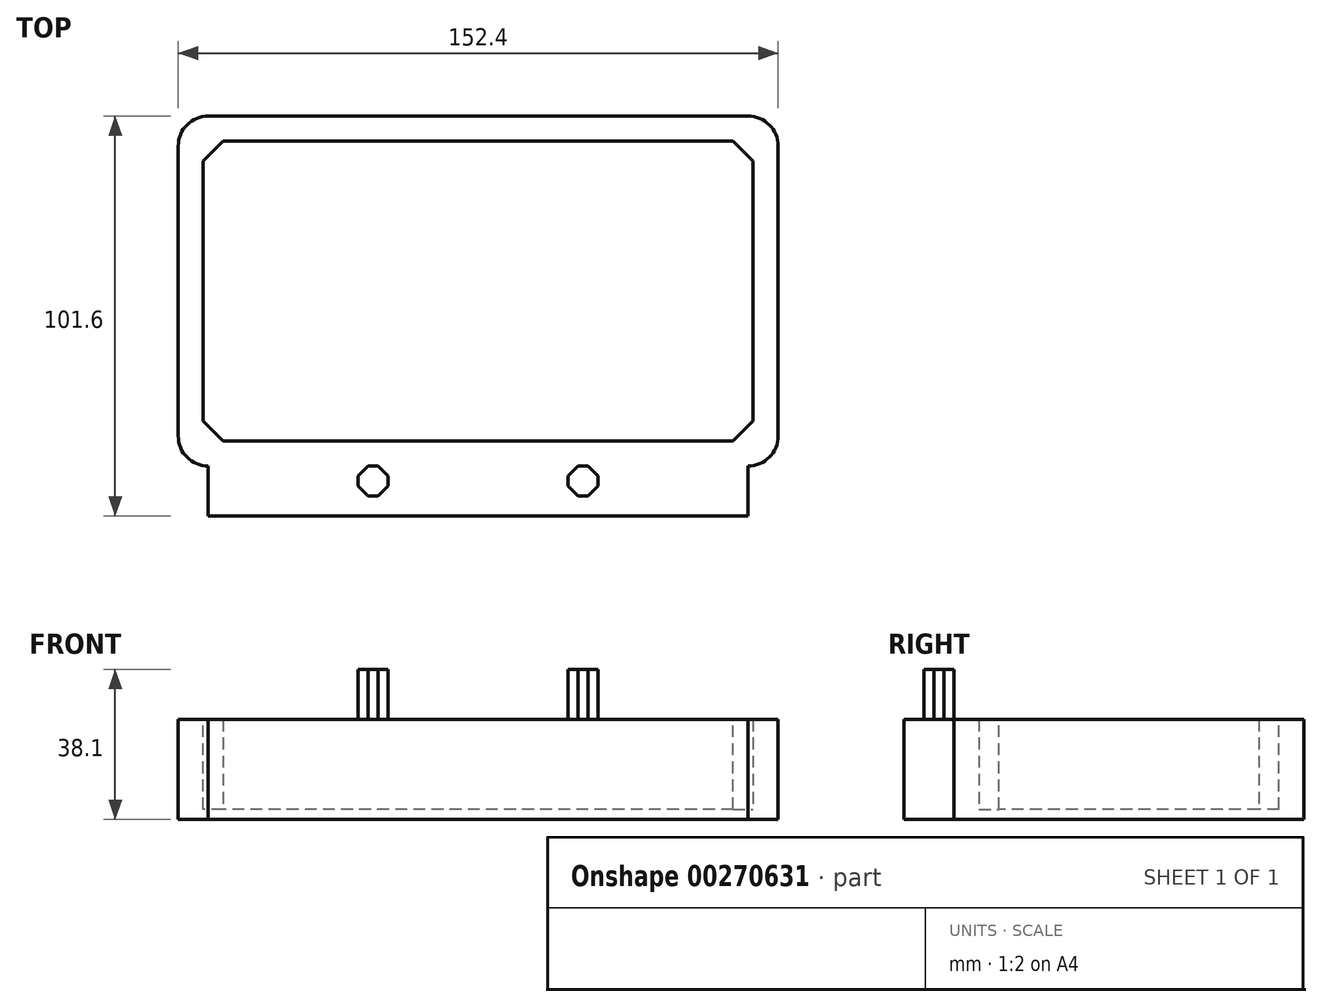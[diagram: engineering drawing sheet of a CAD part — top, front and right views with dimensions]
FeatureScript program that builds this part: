
annotation { "Feature Type Name" : "Feature", "Feature Type Description" : "" }
export const myFeature = defineFeature(function(context is Context, id is Id, definition is map)
    precondition{}
    {
        {
            var Q0;
            Q0=qCreatedBy(makeId("Top.planeOp"),FACE);
            var sketch = newSketch(context, id + "F0", { "sketchPlane" : qUnion([Q0])});
            skLineSegment(sketch, "E0.bottom", {"start": v(68.58, 44.45) * mm, "end": v(-68.58, 44.45) * mm});
            skLineSegment(sketch, "E0.top", {"start": v(68.58, -44.45) * mm, "end": v(-68.58, -44.45) * mm});
            skLineSegment(sketch, "E0.left", {"start": v(76.2, 36.83) * mm, "end": v(76.2, -36.83) * mm});
            skLineSegment(sketch, "E0.right", {"start": v(-76.2, 36.83) * mm, "end": v(-76.2, -36.83) * mm});
            skPoint(sketch, "E0.middle", {"position": v(0, 0) * mm});
            skLineSegment(sketch, "E1.bottom", {"start": v(69.85, 38.1) * mm, "end": v(-69.85, 38.1) * mm});
            skLineSegment(sketch, "E1.top", {"start": v(69.85, -38.1) * mm, "end": v(-69.85, -38.1) * mm});
            skLineSegment(sketch, "E1.left", {"start": v(69.85, 38.1) * mm, "end": v(69.85, -38.1) * mm});
            skLineSegment(sketch, "E1.right", {"start": v(-69.85, 38.1) * mm, "end": v(-69.85, -38.1) * mm});
            skPoint(sketch, "E2.visualSharp", {"position": v(-69.85, 38.1) * mm});
            skPoint(sketch, "E3.visualSharp", {"position": v(-69.85, -38.1) * mm});
            skLineSegment(sketch, "E3.filletArc", {"start": v(-69.85, -38.1) * mm, "end": v(-69.85, -38.1) * mm});
            skPoint(sketch, "E4.visualSharp", {"position": v(69.85, -38.1) * mm});
            skLineSegment(sketch, "E4.filletArc", {"start": v(69.85, -38.1) * mm, "end": v(69.85, -38.1) * mm});
            skPoint(sketch, "E5.visualSharp", {"position": v(69.85, 38.1) * mm});
            skLineSegment(sketch, "E5.filletArc", {"start": v(69.85, 38.1) * mm, "end": v(69.85, 38.1) * mm});
            skPoint(sketch, "E6.visualSharp", {"position": v(-76.2, 44.45) * mm});
            skArc(sketch, "E6.filletArc", {"start": v(-68.58, 44.45) * mm, "mid": v(-73.97, 42.22) * mm, "end": v(-76.2, 36.83) * mm});
            skPoint(sketch, "E7.visualSharp", {"position": v(76.2, 44.45) * mm});
            skArc(sketch, "E7.filletArc", {"start": v(76.2, 36.83) * mm, "mid": v(73.97, 42.22) * mm, "end": v(68.58, 44.45) * mm});
            skPoint(sketch, "E8.visualSharp", {"position": v(-76.2, -44.45) * mm});
            skArc(sketch, "E8.filletArc", {"start": v(-76.2, -36.83) * mm, "mid": v(-73.97, -42.22) * mm, "end": v(-68.58, -44.45) * mm});
            skPoint(sketch, "E9.visualSharp", {"position": v(76.2, -44.45) * mm});
            skArc(sketch, "E9.filletArc", {"start": v(68.58, -44.45) * mm, "mid": v(73.97, -42.22) * mm, "end": v(76.2, -36.83) * mm});
            skSolve(sketch);
        }
        {
            var Q0;
            Q0=makeQuery(id+"F0.imprint","IMPRINT",FACE,{"disambiguationData":[TD([[makeQuery(id+"F0.imprint","IMPRINT",EDGE,{"derivedFrom":sQuery(id+"F0.wireOp",EDGE,"E0.bottom")}),1.0]])]});
            extrude(context, id + "F1", {"entities" : qUnion([Q0]), "depth" : 25.4 * mm});
        }
        {
            var Q0;
            Q0=makeQuery(id+"F1.opExtrude","SWEPT_EDGE",EDGE,{"disambiguationData":[OSD([sQuery(id+"F0.wireOp",EDGE,"E1.bottom"),sQuery(id+"F0.wireOp",EDGE,"E1.right")])]});
            var Q1;
            Q1=makeQuery(id+"F1.opExtrude","SWEPT_EDGE",EDGE,{"disambiguationData":[OSD([sQuery(id+"F0.wireOp",EDGE,"E1.top"),sQuery(id+"F0.wireOp",EDGE,"E1.right")])]});
            var Q2;
            Q2=makeQuery(id+"F1.opExtrude","SWEPT_EDGE",EDGE,{"disambiguationData":[OSD([sQuery(id+"F0.wireOp",EDGE,"E1.bottom"),sQuery(id+"F0.wireOp",EDGE,"E1.left")])]});
            var Q3;
            Q3=makeQuery(id+"F1.opExtrude","SWEPT_EDGE",EDGE,{"disambiguationData":[OSD([sQuery(id+"F0.wireOp",EDGE,"E1.top"),sQuery(id+"F0.wireOp",EDGE,"E1.left")])]});
            chamfer(context, id + "F2", {"entities" : qUnion([Q0, Q1, Q2, Q3]), "width" : 5.08 * mm, "tangentPropagation" : true});
        }
        {
            var Q0;
            Q0=qCreatedBy(makeId("Top.planeOp"),FACE);
            var sketch = newSketch(context, id + "F3", { "sketchPlane" : qUnion([Q0])});
            skLineSegment(sketch, "E10.bottom", {"start": v(-72.19, -40.25) * mm, "end": v(72.1, -40.25) * mm});
            skLineSegment(sketch, "E10.top", {"start": v(-72.19, 41.27) * mm, "end": v(72.1, 41.27) * mm});
            skLineSegment(sketch, "E10.left", {"start": v(-72.19, -40.25) * mm, "end": v(-72.19, 41.27) * mm});
            skLineSegment(sketch, "E10.right", {"start": v(72.1, -40.25) * mm, "end": v(72.1, 41.27) * mm});
            skSolve(sketch);
        }
        {
            var Q0;
            Q0 = qSketchRegion(id + "F3", true);
            extrude(context, id + "F4", {"entities" : qUnion([Q0]), "operationType" : NewBodyOperationType.ADD, "depth" : 2.54 * mm});
        }
        {
            var Q0;
            Q0=makeQuery(id+"F1.opExtrude","SWEPT_FACE",FACE,{"disambiguationData":[OSD([sQuery(id+"F0.wireOp",EDGE,"E0.top")])]});
            extrude(context, id + "F5", {"entities" : qUnion([Q0]), "operationType" : NewBodyOperationType.ADD, "depth" : 12.7 * mm});
        }
        {
            var Q0;
            {var subQ0=sQuery(id+"F0.wireOp",EDGE,"E0.top");Q0=makeQuery(id+"F5.boolean.opBoolean","MERGE",FACE,{"derivedFrom":[makeQuery(id+"F1.opExtrude","CAP_FACE",FACE,{"disambiguationData":[OSD([sQuery(id+"F0.wireOp",EDGE,"E0.bottom"),subQ0,sQuery(id+"F0.wireOp",EDGE,"E0.left"),sQuery(id+"F0.wireOp",EDGE,"E0.right"),sQuery(id+"F0.wireOp",EDGE,"E1.bottom"),sQuery(id+"F0.wireOp",EDGE,"E1.top"),sQuery(id+"F0.wireOp",EDGE,"E1.left"),sQuery(id+"F0.wireOp",EDGE,"E1.right"),sQuery(id+"F0.wireOp",EDGE,"E6.filletArc"),sQuery(id+"F0.wireOp",EDGE,"E7.filletArc"),sQuery(id+"F0.wireOp",EDGE,"E8.filletArc"),sQuery(id+"F0.wireOp",EDGE,"E9.filletArc")])],"isStart":false}),makeQuery(id+"F5.opExtrude","SWEPT_FACE",FACE,{"disambiguationData":[OSD([subQ0]),TDD([makeQuery(id+"F1.opExtrude","CAP_EDGE",EDGE,{"disambiguationData":[OSD([subQ0])],"isStart":false})])]})]});}
            var sketch = newSketch(context, id + "F6", { "sketchPlane" : qUnion([Q0])});
            skLineSegment(sketch, "E11", {"start": v(68.58, -44.45) * mm, "end": v(30.48, -44.45) * mm});
            skLineSegment(sketch, "E12", {"start": v(-68.58, -44.45) * mm, "end": v(-30.48, -44.45) * mm});
            skLineSegment(sketch, "E13.bottom", {"start": v(30.48, -44.45) * mm, "end": v(22.86, -44.45) * mm});
            skLineSegment(sketch, "E13.top", {"start": v(30.48, -52.07) * mm, "end": v(22.86, -52.07) * mm});
            skLineSegment(sketch, "E13.left", {"start": v(30.48, -44.45) * mm, "end": v(30.48, -52.07) * mm});
            skLineSegment(sketch, "E13.right", {"start": v(22.86, -44.45) * mm, "end": v(22.86, -52.07) * mm});
            skLineSegment(sketch, "E14.bottom", {"start": v(-30.48, -44.45) * mm, "end": v(-22.86, -44.45) * mm});
            skLineSegment(sketch, "E14.top", {"start": v(-30.48, -52.07) * mm, "end": v(-22.86, -52.07) * mm});
            skLineSegment(sketch, "E14.left", {"start": v(-30.48, -44.45) * mm, "end": v(-30.48, -52.07) * mm});
            skLineSegment(sketch, "E14.right", {"start": v(-22.86, -44.45) * mm, "end": v(-22.86, -52.07) * mm});
            skSolve(sketch);
        }
        {
            var Q0;
            Q0=makeQuery(id+"F6.imprint","IMPRINT",FACE,{"disambiguationData":[TD([[makeQuery(id+"F6.imprint","IMPRINT",EDGE,{"derivedFrom":sQuery(id+"F6.wireOp",EDGE,"E13.bottom")}),1.0]])]});
            var Q1;
            Q1=makeQuery(id+"F6.imprint","IMPRINT",FACE,{"disambiguationData":[TD([[makeQuery(id+"F6.imprint","IMPRINT",EDGE,{"derivedFrom":sQuery(id+"F6.wireOp",EDGE,"E14.bottom")}),-1.0]])]});
            extrude(context, id + "F7", {"entities" : qUnion([Q0, Q1]), "operationType" : NewBodyOperationType.ADD, "depth" : 12.7 * mm});
        }
        {
            var Q0;
            Q0=makeQuery(id+"F7.opExtrude","SWEPT_EDGE",EDGE,{"disambiguationData":[OSD([sQuery(id+"F6.wireOp",EDGE,"E13.bottom"),sQuery(id+"F6.wireOp",EDGE,"E13.left")])]});
            chamfer(context, id + "F8", {"entities" : qUnion([Q0]), "width" : 2.54 * mm, "tangentPropagation" : true});
        }
        {
            var Q0;
            Q0=makeQuery(id+"F7.opExtrude","SWEPT_EDGE",EDGE,{"disambiguationData":[OSD([sQuery(id+"F6.wireOp",EDGE,"E13.bottom"),sQuery(id+"F6.wireOp",EDGE,"E13.right")])]});
            var Q1;
            Q1=makeQuery(id+"F7.opExtrude","SWEPT_EDGE",EDGE,{"disambiguationData":[OSD([sQuery(id+"F6.wireOp",EDGE,"E13.top"),sQuery(id+"F6.wireOp",EDGE,"E13.right")])]});
            chamfer(context, id + "F9", {"entities" : qUnion([Q0, Q1]), "width" : 2.54 * mm, "tangentPropagation" : true});
        }
        {
            var Q0;
            Q0=makeQuery(id+"F7.opExtrude","SWEPT_EDGE",EDGE,{"disambiguationData":[OSD([sQuery(id+"F6.wireOp",EDGE,"E13.top"),sQuery(id+"F6.wireOp",EDGE,"E13.left")])]});
            chamfer(context, id + "F10", {"entities" : qUnion([Q0]), "width" : 2.54 * mm, "tangentPropagation" : true});
        }
        {
            var Q0;
            Q0=makeQuery(id+"F7.opExtrude","SWEPT_EDGE",EDGE,{"disambiguationData":[OSD([sQuery(id+"F6.wireOp",EDGE,"E14.bottom"),sQuery(id+"F6.wireOp",EDGE,"E14.left")])]});
            var Q1;
            Q1=makeQuery(id+"F7.opExtrude","SWEPT_EDGE",EDGE,{"disambiguationData":[OSD([sQuery(id+"F6.wireOp",EDGE,"E14.bottom"),sQuery(id+"F6.wireOp",EDGE,"E14.right")])]});
            var Q2;
            Q2=makeQuery(id+"F7.opExtrude","SWEPT_EDGE",EDGE,{"disambiguationData":[OSD([sQuery(id+"F6.wireOp",EDGE,"E14.top"),sQuery(id+"F6.wireOp",EDGE,"E14.left")])]});
            var Q3;
            Q3=makeQuery(id+"F7.opExtrude","SWEPT_EDGE",EDGE,{"disambiguationData":[OSD([sQuery(id+"F6.wireOp",EDGE,"E14.top"),sQuery(id+"F6.wireOp",EDGE,"E14.right")])]});
            chamfer(context, id + "F11", {"entities" : qUnion([Q0, Q1, Q2, Q3]), "width" : 2.54 * mm, "tangentPropagation" : true});
        }
    });
